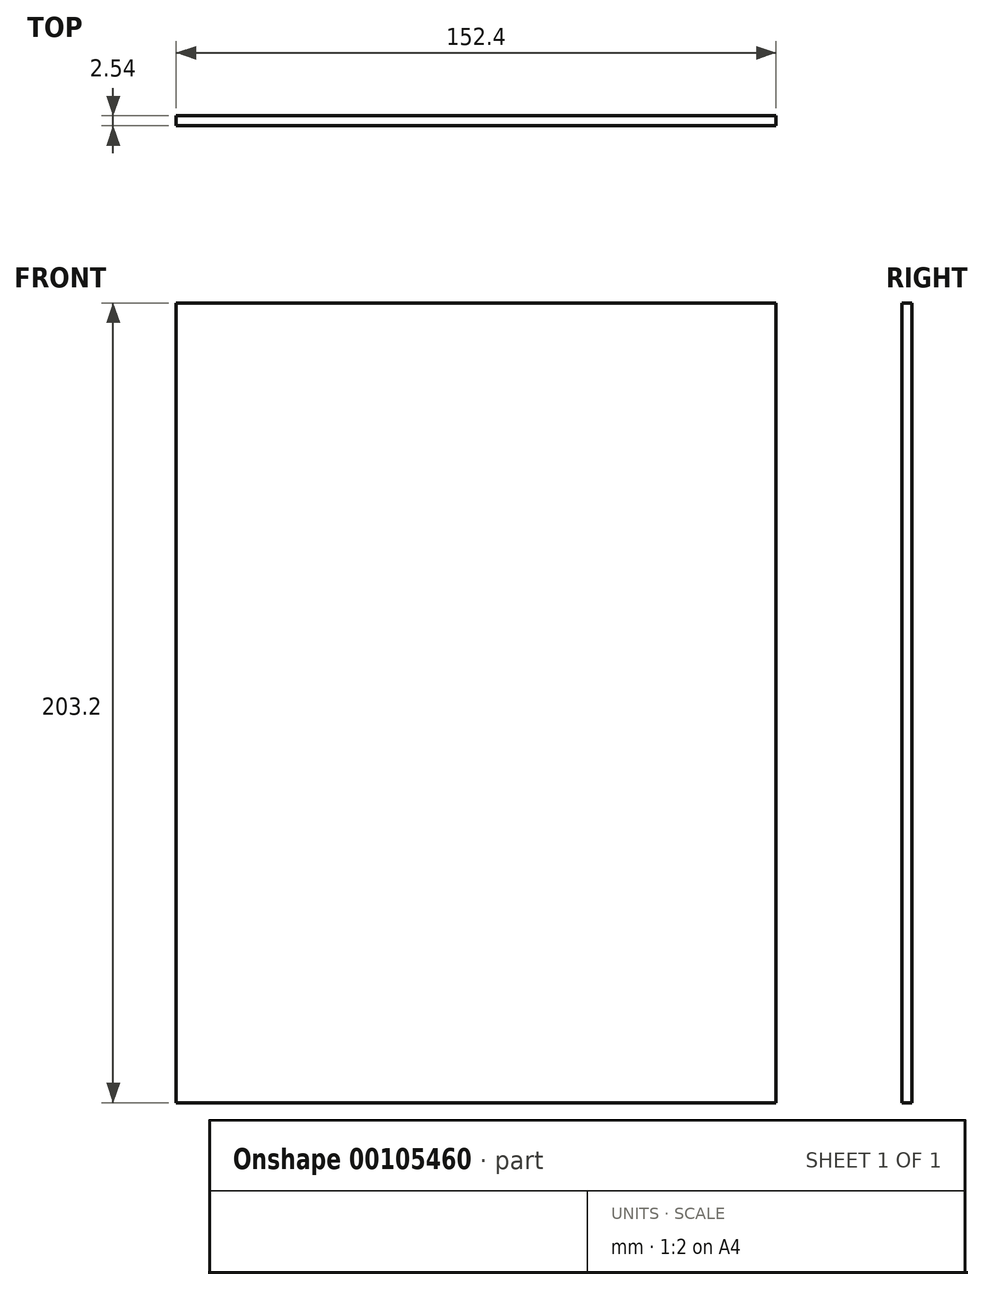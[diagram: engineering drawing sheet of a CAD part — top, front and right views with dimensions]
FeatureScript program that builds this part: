
annotation { "Feature Type Name" : "Feature", "Feature Type Description" : "" }
export const myFeature = defineFeature(function(context is Context, id is Id, definition is map)
    precondition{}
    {
        {
            var Q0;
            Q0=qCreatedBy(makeId("Front.planeOp"),FACE);
            var sketch = newSketch(context, id + "F0", { "sketchPlane" : qUnion([Q0])});
            skLineSegment(sketch, "E0.bottom", {"start": v(-77.13, 170.85) * mm, "end": v(75.27, 170.85) * mm});
            skLineSegment(sketch, "E0.top", {"start": v(-77.13, -32.35) * mm, "end": v(75.27, -32.35) * mm});
            skLineSegment(sketch, "E0.left", {"start": v(-77.13, 170.85) * mm, "end": v(-77.13, -32.35) * mm});
            skLineSegment(sketch, "E0.right", {"start": v(75.27, 170.85) * mm, "end": v(75.27, -32.35) * mm});
            skSolve(sketch);
        }
        {
            var Q0;
            Q0 = qSketchRegion(id + "F0", true);
            extrude(context, id + "F1", {"entities" : qUnion([Q0]), "depth" : 2.54 * mm});
        }
    });
